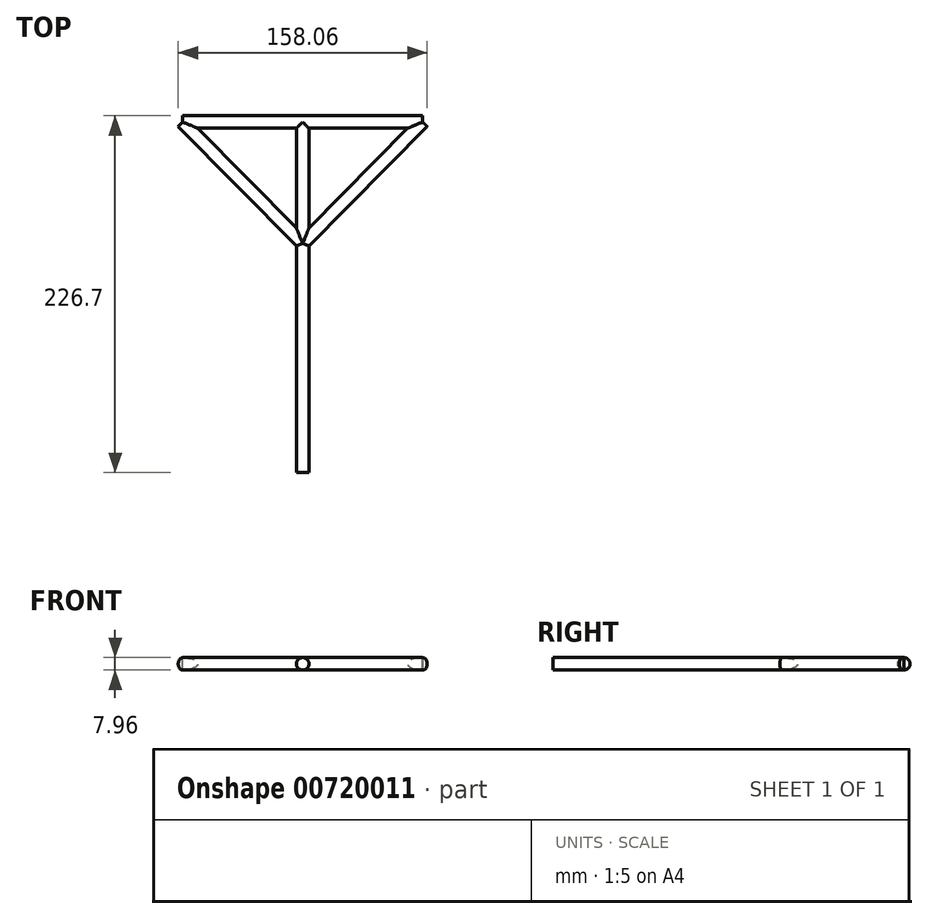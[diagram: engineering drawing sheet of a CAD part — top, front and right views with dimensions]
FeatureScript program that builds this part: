
annotation { "Feature Type Name" : "Feature", "Feature Type Description" : "" }
export const myFeature = defineFeature(function(context is Context, id is Id, definition is map)
    precondition{}
    {
        {
            var Q0;
            Q0=qCreatedBy(makeId("Top.planeOp"),FACE);
            var sketch = newSketch(context, id + "F0", { "sketchPlane" : qUnion([Q0])});
            skLineSegment(sketch, "E0", {"start": v(0, 0) * mm, "end": v(76.2, 0) * mm});
            skLineSegment(sketch, "E1", {"start": v(0, 0) * mm, "end": v(-76.2, 0) * mm});
            skLineSegment(sketch, "E2", {"start": v(-76.2, 0) * mm, "end": v(0, -77.11) * mm});
            skLineSegment(sketch, "E3", {"start": v(0, -77.11) * mm, "end": v(76.2, 0) * mm});
            skLineSegment(sketch, "E4", {"start": v(0, 0) * mm, "end": v(0, -77.11) * mm});
            skLineSegment(sketch, "E5", {"start": v(0, -77.11) * mm, "end": v(0, -222.72) * mm});
            skSolve(sketch);
        }
        {
            var Q0;
            Q0=sQuery(id+"F0.wireOp",EDGE,"E1");
            extrude(context, id + "F1", {"bodyType" : ToolBodyType.SURFACE, "surfaceEntities" : qUnion([Q0]), "depth" : 3.98 * mm, "offsetDistance" : 25.4 * mm});
        }
        {
            var Q0;
            Q0=makeQuery(id+"F1.opExtrude","SWEPT_FACE",FACE,{"disambiguationData":[OSD([sQuery(id+"F0.wireOp",EDGE,"E1")])]});
            var Q1;
            Q1=sQuery(id+"F0.wireOp",EDGE,"E1");
            revolve(context, id + "F2", {"surfaceOperationType" : NewSurfaceOperationType.NEW, "entities" : qUnion([Q0]), "axis" : qUnion([Q1]), "revolveType" : RevolveType.FULL});
        }
        {
            var Q0;
            Q0=sQuery(id+"F0.wireOp",EDGE,"E0");
            extrude(context, id + "F3", {"bodyType" : ToolBodyType.SURFACE, "surfaceEntities" : qUnion([Q0]), "depth" : 3.98 * mm, "offsetDistance" : 25.4 * mm});
        }
        {
            var Q0;
            Q0=makeQuery(id+"F3.opExtrude","SWEPT_FACE",FACE,{"disambiguationData":[OSD([sQuery(id+"F0.wireOp",EDGE,"E0")])]});
            var Q1;
            Q1=sQuery(id+"F0.wireOp",EDGE,"E0");
            revolve(context, id + "F4", {"operationType" : NewBodyOperationType.ADD, "surfaceOperationType" : NewSurfaceOperationType.NEW, "entities" : qUnion([Q0]), "axis" : qUnion([Q1]), "revolveType" : RevolveType.FULL});
        }
        {
            var Q0;
            Q0=sQuery(id+"F0.wireOp",EDGE,"E3");
            extrude(context, id + "F5", {"bodyType" : ToolBodyType.SURFACE, "surfaceEntities" : qUnion([Q0]), "depth" : 3.98 * mm, "offsetDistance" : 25.4 * mm});
        }
        {
            var Q0;
            Q0=makeQuery(id+"F5.opExtrude","SWEPT_FACE",FACE,{"disambiguationData":[OSD([sQuery(id+"F0.wireOp",EDGE,"E3")])]});
            var Q1;
            Q1=sQuery(id+"F0.wireOp",EDGE,"E3");
            revolve(context, id + "F6", {"operationType" : NewBodyOperationType.ADD, "surfaceOperationType" : NewSurfaceOperationType.NEW, "entities" : qUnion([Q0]), "axis" : qUnion([Q1]), "revolveType" : RevolveType.FULL});
        }
        {
            var Q0;
            Q0=sQuery(id+"F0.wireOp",EDGE,"E2");
            extrude(context, id + "F7", {"bodyType" : ToolBodyType.SURFACE, "surfaceEntities" : qUnion([Q0]), "depth" : 3.98 * mm, "offsetDistance" : 25.4 * mm});
        }
        {
            var Q0;
            Q0=makeQuery(id+"F7.opExtrude","SWEPT_FACE",FACE,{"disambiguationData":[OSD([sQuery(id+"F0.wireOp",EDGE,"E2")])]});
            var Q1;
            Q1=sQuery(id+"F0.wireOp",EDGE,"E2");
            revolve(context, id + "F8", {"operationType" : NewBodyOperationType.ADD, "surfaceOperationType" : NewSurfaceOperationType.NEW, "entities" : qUnion([Q0]), "axis" : qUnion([Q1]), "revolveType" : RevolveType.FULL});
        }
        {
            var Q0;
            Q0=sQuery(id+"F0.wireOp",EDGE,"E4");
            extrude(context, id + "F9", {"bodyType" : ToolBodyType.SURFACE, "surfaceEntities" : qUnion([Q0]), "depth" : 3.98 * mm, "offsetDistance" : 25.4 * mm});
        }
        {
            var Q0;
            Q0=makeQuery(id+"F9.opExtrude","SWEPT_FACE",FACE,{"disambiguationData":[OSD([sQuery(id+"F0.wireOp",EDGE,"E4")])]});
            var Q1;
            Q1=sQuery(id+"F0.wireOp",EDGE,"E4");
            revolve(context, id + "F10", {"operationType" : NewBodyOperationType.ADD, "surfaceOperationType" : NewSurfaceOperationType.NEW, "entities" : qUnion([Q0]), "axis" : qUnion([Q1]), "revolveType" : RevolveType.FULL});
        }
        {
            var Q0;
            Q0=sQuery(id+"F0.wireOp",EDGE,"E5");
            extrude(context, id + "F11", {"bodyType" : ToolBodyType.SURFACE, "surfaceEntities" : qUnion([Q0]), "depth" : 3.98 * mm, "offsetDistance" : 25.4 * mm});
        }
        {
            var Q0;
            Q0=makeQuery(id+"F11.opExtrude","SWEPT_FACE",FACE,{"disambiguationData":[OSD([sQuery(id+"F0.wireOp",EDGE,"E5")])]});
            var Q1;
            Q1=sQuery(id+"F0.wireOp",EDGE,"E5");
            revolve(context, id + "F12", {"operationType" : NewBodyOperationType.ADD, "surfaceOperationType" : NewSurfaceOperationType.NEW, "entities" : qUnion([Q0]), "axis" : qUnion([Q1]), "revolveType" : RevolveType.FULL});
        }
    });
